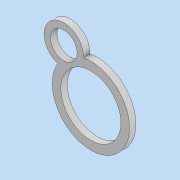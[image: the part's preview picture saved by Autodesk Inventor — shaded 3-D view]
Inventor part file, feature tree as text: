
AUTODESK INVENTOR PART (.ipt)
format: ipt  version: 2022 (Build 260153070, 153G)  size: 1,709,056 bytes
history: native  units: mm
features: other x7, extrude x1, sketch x1
ambient origin geometry x8: Origin, YZ Plane, XZ Plane, XY Plane, X Axis, Y Axis, Z Axis, Center Point
bodies: Body1 (feature_tree), Body2 (feature_tree)
feature tree (9):
  other  "P00173-09-004.ipt"
  extrude  "Extrusion2"  Depth=1.5mm
  other  "Side"
  other  "Bottom"
  other  "Legs"
  sketch  "Sketch4"  dims[d0=10.0mm d81=2.0mm d82=2.0mm d83=2.0mm d3=6.2mm d4=1.5mm d5=6.108652mm d6=11.0mm d7=1.5mm d8=0.0mm]
  other  "TaggingFeature1"
  other  "Solid6::P00173-09-004.ipt"
  other  "Srf1"
